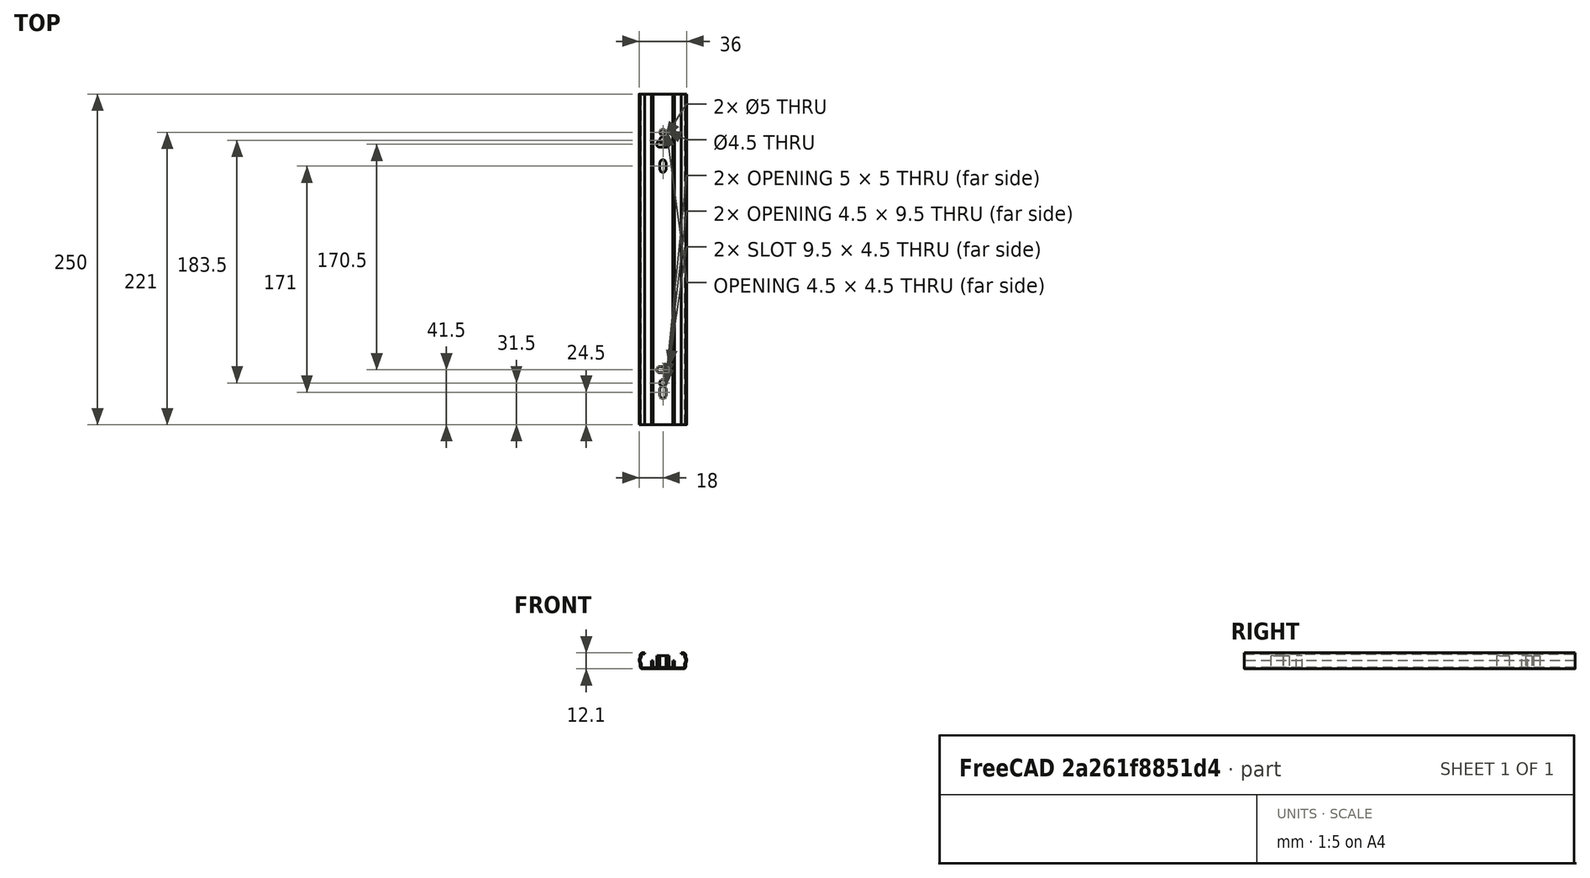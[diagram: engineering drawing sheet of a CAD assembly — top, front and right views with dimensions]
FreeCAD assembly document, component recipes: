
FREECAD ASSEMBLY — COMPONENT RECIPES ("rails")

This assembly document has 2 components, labeled P0..P1 below (a component is one placed body or linked part). 2 of them carry a construction recipe — the FreeCAD feature program that regenerates the part from scratch, quoted from this document or its linked companion documents; the rest are supplied as boundary geometry only. No exploded tour is included for this assembly.
COMPONENT P0 — recipe-attached ("Body002", modeled in this document).
Construction recipe (the document's own serialized feature program — sketch geometry with constraints, then the solid features built on it; lengths are millimeters unless a unit is written):

FEATURE [PartDesign::SubShapeBinder] Binder
  BindCopyOnChange = 0
  BindMode = 0
  ClaimChildren = true
  Context = -> Body [Binder.]
  Fuse = false
  MakeFace = true
  OffsetFill = false
  OffsetIntersection = false
  OffsetJoinType = 0
  OffsetOpenResult = false
  PartialLoad = false
  Placement = pos=(0,0,0) rot=(0,0.707107,0.707107;3.14159rad)
  Relative = false
  Support = -> [Connect]
  _Version = 2
FEATURE [PartDesign::FeaturePython] BaseBend  # WARN: FeaturePython — macro-defined, semantics opaque (R4)
  BendSide = 1
  BendSketch = -> Binder
  MidPlane = false
  Reverse = false
  Suppressed = false
  length = 250
  radius = 1
  thickness = 0.8
FEATURE [PartDesign::Boolean] Boolean
  BaseFeature = -> BaseBend
  Group = -> [Compound]
  Refine = true
  Suppressed = false
  Type = 1
  UsePlacement = true
FEATURE [PartDesign::CoordinateSystem] Local_CS
  AttacherType = Attacher::AttachEngine3D
  AttachmentSupport = -> [XY_Plane]
  MapMode = 5
FEATURE [PartDesign::CoordinateSystem] Local_CS002
  AttacherType = Attacher::AttachEngine3D
  AttachmentOffset = pos=(0,0,12) rot=(0,1,0;3.14159rad)
  AttachmentSupport = -> [XY_Plane]
  MapMode = 5
  Placement = pos=(0,0,12) rot=(0,1,0;3.14159rad)
FEATURE [PartDesign::Body] Body
  Group = -> [Binder,BaseBend,Boolean,Local_CS,Local_CS002]
  Origin = -> Origin
  Tip = -> Boolean
COMPONENT P1 — recipe-attached ("Body003", modeled in this document).
Construction recipe (the document's own serialized feature program — sketch geometry with constraints, then the solid features built on it; lengths are millimeters unless a unit is written):

FEATURE [PartDesign::SubShapeBinder] Binder001
  BindCopyOnChange = 0
  BindMode = 0
  ClaimChildren = true
  Context = -> Body001 [Binder001.]
  Fuse = false
  MakeFace = true
  OffsetFill = false
  OffsetIntersection = false
  OffsetJoinType = 0
  OffsetOpenResult = false
  PartialLoad = false
  Placement = pos=(0,0,0) rot=(1,0,0;1.5708rad)
  Relative = false
  Support = -> [Connect001]
  _Version = 2
FEATURE [PartDesign::FeaturePython] BaseBend001  # WARN: FeaturePython — macro-defined, semantics opaque (R4)
  BendSide = 1
  BendSketch = -> Binder001
  MidPlane = false
  Reverse = true
  Suppressed = false
  length = 250
  radius = 1
  thickness = 1
FEATURE [PartDesign::Boolean] Boolean001
  BaseFeature = -> BaseBend001
  Group = -> [Extrude001]
  Refine = true
  Suppressed = false
  Type = 1
  UsePlacement = true
FEATURE [PartDesign::CoordinateSystem] Local_CS001
  AttacherType = Attacher::AttachEngine3D
  AttachmentSupport = -> [XY_Plane001]
  MapMode = 5
FEATURE [PartDesign::Body] Body001
  Group = -> [Binder001,BaseBend001,Boolean001,Local_CS001]
  Origin = -> Origin001
  Tip = -> Boolean001
PROVENANCE & LICENSES
A FreeCAD (.FCStd) document from a public repository crawl; recipes are the document's own serialized feature recipes (and, for linked parts, companion documents' recipes).
License: as declared in the source repository (recorded in the dataset sidecar).
